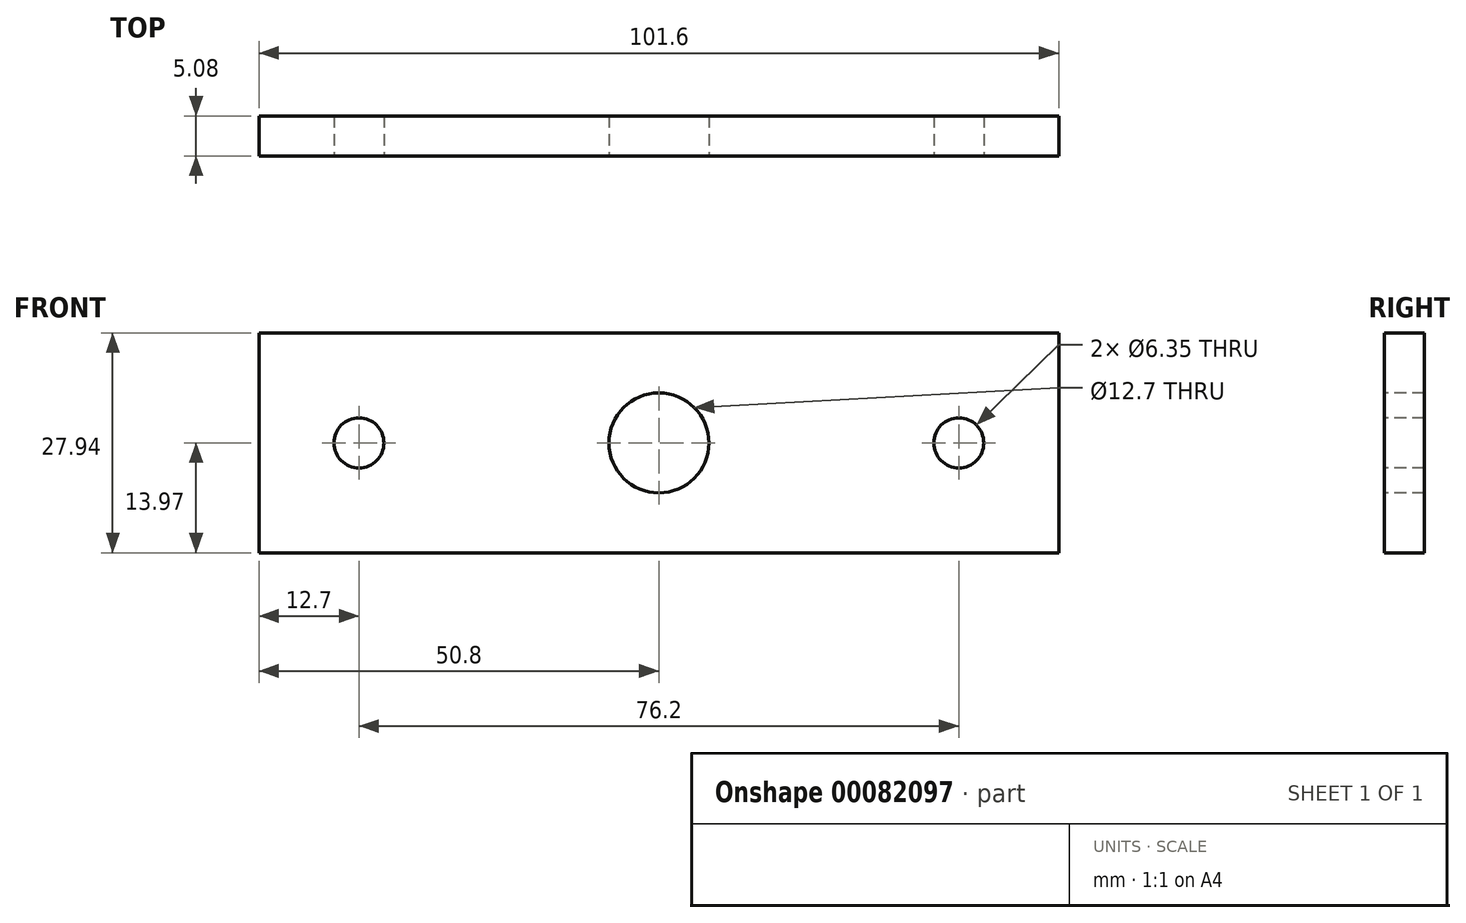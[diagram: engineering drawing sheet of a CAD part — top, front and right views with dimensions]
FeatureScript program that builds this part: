
annotation { "Feature Type Name" : "Feature", "Feature Type Description" : "" }
export const myFeature = defineFeature(function(context is Context, id is Id, definition is map)
    precondition{}
    {
        {
            var Q0;
            Q0=qCreatedBy(makeId("Front.planeOp"),FACE);
            var sketch = newSketch(context, id + "F0", { "sketchPlane" : qUnion([Q0])});
            skLineSegment(sketch, "E0.bottom", {"start": v(-50.8, 13.97) * mm, "end": v(50.8, 13.97) * mm});
            skLineSegment(sketch, "E0.top", {"start": v(-50.8, -13.97) * mm, "end": v(50.8, -13.97) * mm});
            skLineSegment(sketch, "E0.left", {"start": v(-50.8, 13.97) * mm, "end": v(-50.8, -13.97) * mm});
            skLineSegment(sketch, "E0.right", {"start": v(50.8, 13.97) * mm, "end": v(50.8, -13.97) * mm});
            skPoint(sketch, "E0.middle", {"position": v(0, 0) * mm});
            skSolve(sketch);
        }
        {
            var Q0;
            Q0=makeQuery(id+"F0.imprint","IMPRINT",FACE,{"disambiguationData":[TD([[makeQuery(id+"F0.imprint","IMPRINT",EDGE,{"derivedFrom":sQuery(id+"F0.wireOp",EDGE,"E0.bottom")}),-1.0]])]});
            extrude(context, id + "F1", {"entities" : qUnion([Q0]), "depth" : 5.08 * mm});
        }
        {
            var Q0;
            Q0=makeQuery(id+"F1.opExtrude","CAP_FACE",FACE,{"disambiguationData":[OSD([sQuery(id+"F0.wireOp",EDGE,"E0.bottom"),sQuery(id+"F0.wireOp",EDGE,"E0.top"),sQuery(id+"F0.wireOp",EDGE,"E0.left"),sQuery(id+"F0.wireOp",EDGE,"E0.right")])],"isStart":false});
            var sketch = newSketch(context, id + "F2", { "sketchPlane" : qUnion([Q0])});
            skPoint(sketch, "E1", {"position": v(-38.1, 0) * mm});
            skPoint(sketch, "E2", {"position": v(38.1, 0) * mm});
            skSolve(sketch);
        }
        {
            var Q0;
            Q0=sQuery(id+"F2.wireOp",VERTEX,"E1");
            var Q1;
            Q1=sQuery(id+"F2.wireOp",VERTEX,"E2");
            var Q2;
            Q2=makeQuery(id+"F1.opExtrude","SWEPT_BODY",BODY,{"disambiguationData":[OSD([sQuery(id+"F0.wireOp",EDGE,"E0.bottom"),sQuery(id+"F0.wireOp",EDGE,"E0.top"),sQuery(id+"F0.wireOp",EDGE,"E0.left"),sQuery(id+"F0.wireOp",EDGE,"E0.right")])]});
            hole(context, id + "F3", {"style" : HoleStyle.SIMPLE, "endStyle" : HoleEndStyle.THROUGH, "holeDiameter" : 6.35 * mm, "locations" : qUnion([Q0, Q1]), "scope" : qUnion([Q2]), "isTappedThrough" : true});
        }
        {
            var Q0;
            Q0=makeQuery(id+"F1.opExtrude","CAP_FACE",FACE,{"disambiguationData":[OSD([sQuery(id+"F0.wireOp",EDGE,"E0.bottom"),sQuery(id+"F0.wireOp",EDGE,"E0.top"),sQuery(id+"F0.wireOp",EDGE,"E0.left"),sQuery(id+"F0.wireOp",EDGE,"E0.right")])],"isStart":false});
            var sketch = newSketch(context, id + "F4", { "sketchPlane" : qUnion([Q0])});
            skPoint(sketch, "E3", {"position": v(0, 0) * mm});
            skSolve(sketch);
        }
        {
            var Q0;
            Q0=sQuery(id+"F4.wireOp",VERTEX,"E3");
            var Q1;
            Q1=makeQuery(id+"F1.opExtrude","SWEPT_BODY",BODY,{"disambiguationData":[OSD([sQuery(id+"F0.wireOp",EDGE,"E0.bottom"),sQuery(id+"F0.wireOp",EDGE,"E0.top"),sQuery(id+"F0.wireOp",EDGE,"E0.left"),sQuery(id+"F0.wireOp",EDGE,"E0.right")])]});
            hole(context, id + "F5", {"style" : HoleStyle.SIMPLE, "endStyle" : HoleEndStyle.THROUGH, "holeDiameter" : 12.7 * mm, "locations" : qUnion([Q0]), "scope" : qUnion([Q1]), "isTappedThrough" : true});
        }
    });
